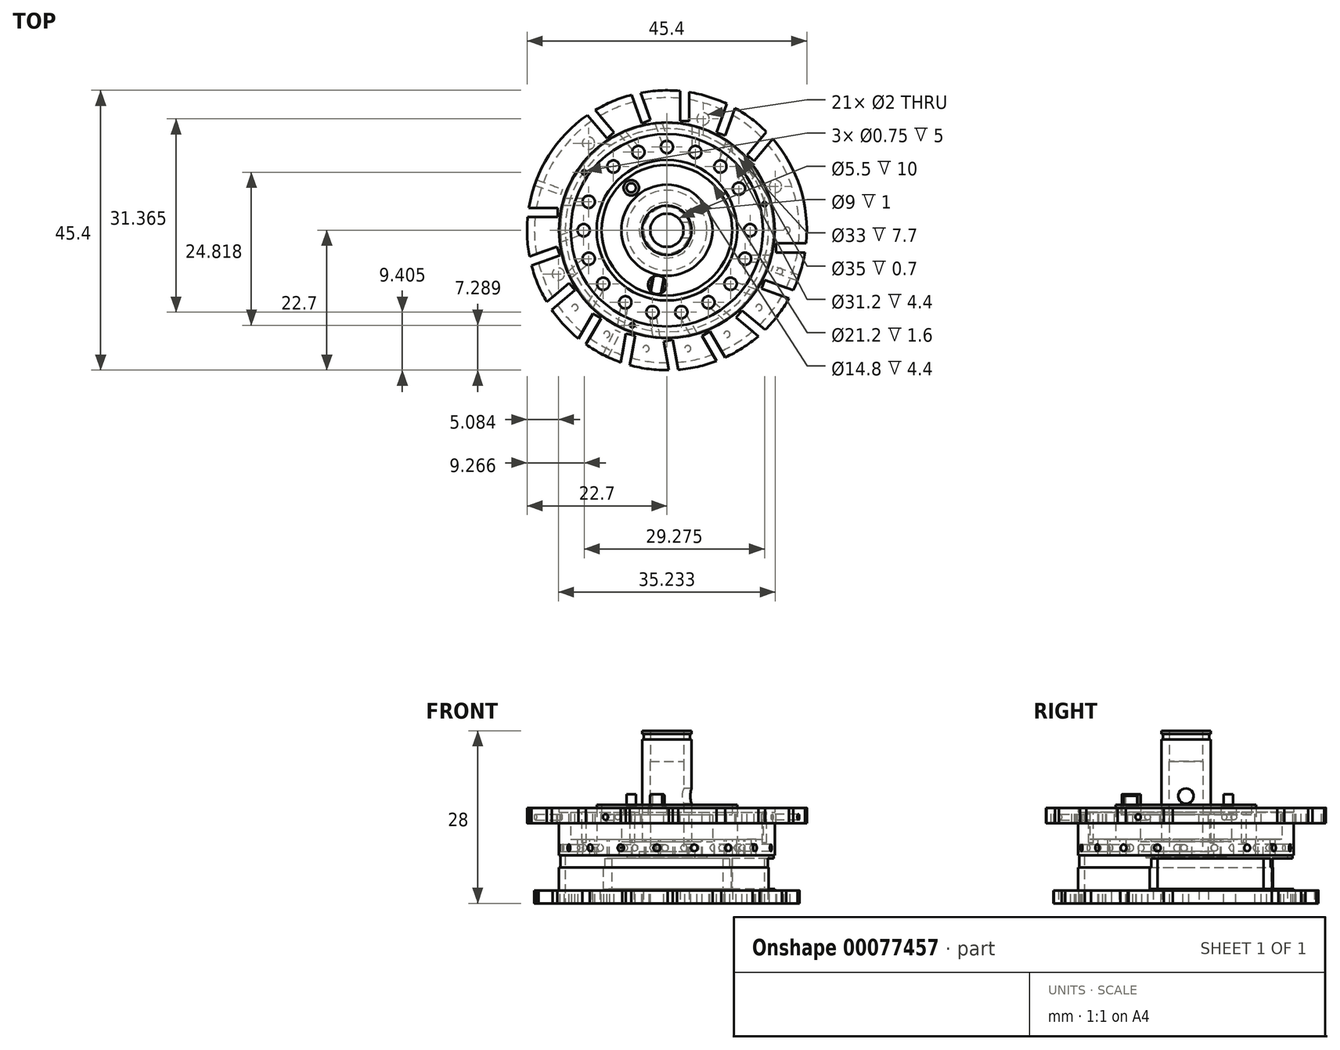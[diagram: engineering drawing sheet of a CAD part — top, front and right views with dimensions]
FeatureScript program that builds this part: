
annotation { "Feature Type Name" : "Feature", "Feature Type Description" : "" }
export const myFeature = defineFeature(function(context is Context, id is Id, definition is map)
    precondition{}
    {
        {
            var Q0;
            Q0=qCreatedBy(makeId("Front.planeOp"),FACE);
            var sketch = newSketch(context, id + "F0", { "sketchPlane" : qUnion([Q0])});
            skLineSegment(sketch, "E0", {"start": v(4, 20.6) * mm, "end": v(4, 20.1) * mm});
            skLineSegment(sketch, "E1", {"start": v(4, 20.1) * mm, "end": v(3.75, 20.1) * mm});
            skLineSegment(sketch, "E2", {"start": v(3.75, 20.1) * mm, "end": v(3.75, 19.2) * mm});
            skLineSegment(sketch, "E3", {"start": v(3.75, 19.2) * mm, "end": v(4, 19.2) * mm});
            skLineSegment(sketch, "E4", {"start": v(4, 19.2) * mm, "end": v(4, 2.6) * mm});
            skLineSegment(sketch, "E5", {"start": v(4, 2.6) * mm, "end": v(7.4, 2.6) * mm});
            skLineSegment(sketch, "E6", {"start": v(7.4, 2.6) * mm, "end": v(7.4, 7) * mm});
            skLineSegment(sketch, "E7", {"start": v(7.4, 7) * mm, "end": v(10.6, 7) * mm});
            skLineSegment(sketch, "E8", {"start": v(10.6, 7) * mm, "end": v(10.6, 8.6) * mm});
            skLineSegment(sketch, "E9", {"start": v(10.6, 8.6) * mm, "end": v(11.4, 8.6) * mm});
            skLineSegment(sketch, "E10", {"start": v(11.4, 8.6) * mm, "end": v(11.4, 3) * mm});
            skLineSegment(sketch, "E11", {"start": v(11.4, 3) * mm, "end": v(15.6, 3) * mm});
            skLineSegment(sketch, "E12", {"start": v(15.6, 3) * mm, "end": v(15.6, 7.4) * mm});
            skLineSegment(sketch, "E13", {"start": v(15.6, 7.4) * mm, "end": v(17.5, 7.4) * mm});
            skLineSegment(sketch, "E14", {"start": v(17.5, 7.4) * mm, "end": v(17.5, 8.1) * mm});
            skLineSegment(sketch, "E15", {"start": v(17.5, 8.1) * mm, "end": v(22.7, 8.1) * mm});
            skLineSegment(sketch, "E16", {"start": v(22.7, 8.1) * mm, "end": v(22.7, 5.6) * mm});
            skLineSegment(sketch, "E17", {"start": v(22.7, 5.6) * mm, "end": v(17.5, 5.6) * mm});
            skLineSegment(sketch, "E18", {"start": v(17.5, 5.6) * mm, "end": v(17.5, 0.4) * mm});
            skLineSegment(sketch, "E19", {"start": v(17.5, 0.4) * mm, "end": v(17.3, 0.4) * mm});
            skLineSegment(sketch, "E20", {"start": v(17.3, 0.4) * mm, "end": v(17.3, -1.6) * mm});
            skLineSegment(sketch, "E21", {"start": v(17.3, -1.6) * mm, "end": v(17.5, -1.6) * mm});
            skLineSegment(sketch, "E22", {"start": v(17.5, -1.6) * mm, "end": v(17.5, -5.3) * mm});
            skLineSegment(sketch, "E23", {"start": v(17.5, -5.3) * mm, "end": v(21.5, -5.3) * mm});
            skLineSegment(sketch, "E24", {"start": v(21.5, -5.3) * mm, "end": v(21.5, -7.4) * mm});
            skLineSegment(sketch, "E25", {"start": v(21.5, -7.4) * mm, "end": v(16.5, -7.4) * mm});
            skLineSegment(sketch, "E26", {"start": v(16.5, -7.4) * mm, "end": v(16.5, 0.3) * mm});
            skLineSegment(sketch, "E27", {"start": v(16.5, 0.3) * mm, "end": v(6.5, 0.3) * mm});
            skLineSegment(sketch, "E28", {"start": v(6.5, 0.3) * mm, "end": v(6.5, 0) * mm});
            skLineSegment(sketch, "E29", {"start": v(6.5, 0) * mm, "end": v(4.5, 0) * mm});
            skLineSegment(sketch, "E30", {"start": v(4.5, 0) * mm, "end": v(4.5, 1) * mm});
            skLineSegment(sketch, "E31", {"start": v(4.5, 1) * mm, "end": v(2.7, 1) * mm});
            skLineSegment(sketch, "E32", {"start": v(2.7, 1) * mm, "end": v(2.7, 5.6) * mm});
            skLineSegment(sketch, "E33", {"start": v(2.7, 5.6) * mm, "end": v(2.75, 5.6) * mm});
            skLineSegment(sketch, "E34", {"start": v(2.75, 5.6) * mm, "end": v(2.75, 15.6) * mm});
            skLineSegment(sketch, "E35", {"start": v(2.75, 15.6) * mm, "end": v(2.7, 15.6) * mm});
            skLineSegment(sketch, "E36", {"start": v(2.7, 15.6) * mm, "end": v(2.7, 20.6) * mm});
            skLineSegment(sketch, "E37", {"start": v(2.7, 20.6) * mm, "end": v(4, 20.6) * mm});
            skLineSegment(sketch, "E38", {"start": v(0, 0) * mm, "end": v(0, 20.6) * mm, "construction": true});
            skSolve(sketch);
        }
        {
            var Q0;
            Q0=makeQuery(id+"F0.imprint","IMPRINT",FACE,{"disambiguationData":[TD([[makeQuery(id+"F0.imprint","IMPRINT",EDGE,{"derivedFrom":sQuery(id+"F0.wireOp",EDGE,"E0")}),-1.0]])]});
            var Q1;
            Q1=sQuery(id+"F0.wireOp",EDGE,"E38");
            revolve(context, id + "F1", {"entities" : qUnion([Q0]), "axis" : qUnion([Q1]), "revolveType" : RevolveType.FULL});
        }
        {
            var Q0;
            Q0=makeQuery(id+"F1.opRevolve","SWEPT_FACE",FACE,{"disambiguationData":[OSD([sQuery(id+"F0.wireOp",EDGE,"E15")])]});
            var sketch = newSketch(context, id + "F2", { "sketchPlane" : qUnion([Q0])});
            skLineSegment(sketch, "E39.bottom", {"start": v(24.7, -2.13) * mm, "end": v(17.7, -2.13) * mm});
            skLineSegment(sketch, "E39.top", {"start": v(24.7, -3.63) * mm, "end": v(17.7, -3.63) * mm});
            skLineSegment(sketch, "E39.left", {"start": v(24.7, -2.13) * mm, "end": v(24.7, -3.63) * mm});
            skLineSegment(sketch, "E39.right", {"start": v(17.7, -2.13) * mm, "end": v(17.7, -3.63) * mm});
            skLineSegment(sketch, "E40", {"start": v(14.9, -4.63) * mm, "end": v(24.7, -4.63) * mm, "construction": true});
            skLineSegment(sketch, "E41", {"start": v(0, 0) * mm, "end": v(21.33, -7.76) * mm, "construction": true});
            skPoint(sketch, "E42", {"position": v(12.69, -4.62) * mm});
            skCircle(sketch, "E43", {"center": v(12.69, -4.62) * mm, "radius": 1 * mm});
            skLineSegment(sketch, "E44", {"start": v(14.9, -4.63) * mm, "end": v(13.69, -4.63) * mm, "construction": true});
            skSolve(sketch);
        }
        {
            var Q0;
            Q0=makeQuery(id+"F2.imprint","IMPRINT",FACE,{"disambiguationData":[TD([[makeQuery(id+"F2.imprint","IMPRINT",EDGE,{"derivedFrom":sQuery(id+"F2.wireOp",EDGE,"E43")}),1.0]])]});
            var Q1;
            {var subQ5=sQuery(id+"F2.wireOp",EDGE,"E39.right");Q1=makeQuery(id+"F2.imprint","IMPRINT",FACE,{"disambiguationData":[TD([[makeQuery(id+"F2.imprint","IMPRINT",EDGE,{"derivedFrom":subQ5}),1.0]])]});}
            extrude(context, id + "F3", {"entities" : qUnion([Q0, Q1]), "oppositeDirection" : true, "depth" : 16 * mm});
        }
        {
            var Q0;
            Q0=makeQuery(id+"F3.opExtrude","SWEPT_BODY",BODY,{"disambiguationData":[OSD([sQuery(id+"F0.wireOp",EDGE,"E15"),sQuery(id+"F0.wireOp",EDGE,"E16"),sQuery(id+"F2.wireOp",EDGE,"E39.bottom"),sQuery(id+"F2.wireOp",EDGE,"E39.top"),sQuery(id+"F2.wireOp",EDGE,"E39.right")])]});
            var Q1;
            Q1=makeQuery(id+"F3.opExtrude","SWEPT_BODY",BODY,{"disambiguationData":[OSD([sQuery(id+"F2.wireOp",EDGE,"E43")])]});
            var Q2;
            Q2=sQuery(id+"F0.wireOp",EDGE,"E38");
            circularPattern(context, id + "F4", {"entities" : qUnion([Q0, Q1]), "axis" : qUnion([Q2]), "angle" : 20 * degree, "instanceCount" : round(10), "oppositeDirection" : true});
        }
        {
            var Q0;
            Q0=makeQuery(id+"F3.opExtrude","SWEPT_BODY",BODY,{"disambiguationData":[OSD([sQuery(id+"F0.wireOp",EDGE,"E15"),sQuery(id+"F0.wireOp",EDGE,"E16"),sQuery(id+"F2.wireOp",EDGE,"E39.bottom"),sQuery(id+"F2.wireOp",EDGE,"E39.top"),sQuery(id+"F2.wireOp",EDGE,"E39.right")])]});
            var Q1;
            Q1=makeQuery(id+"F3.opExtrude","SWEPT_BODY",BODY,{"disambiguationData":[OSD([sQuery(id+"F2.wireOp",EDGE,"E43")])]});
            var Q2;
            Q2=sQuery(id+"F0.wireOp",EDGE,"E38");
            circularPattern(context, id + "F5", {"entities" : qUnion([Q0, Q1]), "axis" : qUnion([Q2]), "angle" : 50 * degree, "instanceCount" : round(2)});
        }
        {
            var Q0;
            Q0=makeQuery(id+"F5.opPattern","COPY",BODY,{"derivedFrom":makeQuery(id+"F3.opExtrude","SWEPT_BODY",BODY,{"disambiguationData":[OSD([sQuery(id+"F2.wireOp",EDGE,"E43")])]}),"instanceName":"1"});
            var Q1;
            Q1=makeQuery(id+"F5.opPattern","COPY",BODY,{"derivedFrom":makeQuery(id+"F3.opExtrude","SWEPT_BODY",BODY,{"disambiguationData":[OSD([sQuery(id+"F0.wireOp",EDGE,"E15"),sQuery(id+"F0.wireOp",EDGE,"E16"),sQuery(id+"F2.wireOp",EDGE,"E39.bottom"),sQuery(id+"F2.wireOp",EDGE,"E39.top"),sQuery(id+"F2.wireOp",EDGE,"E39.right")])]}),"instanceName":"1"});
            var Q2;
            Q2=sQuery(id+"F0.wireOp",EDGE,"E38");
            circularPattern(context, id + "F6", {"entities" : qUnion([Q0, Q1]), "axis" : qUnion([Q2]), "angle" : 20 * degree, "instanceCount" : round(5)});
        }
        {
            var Q0;
            Q0=makeQuery(id+"F6.opPattern","COPY",BODY,{"derivedFrom":makeQuery(id+"F5.opPattern","COPY",BODY,{"derivedFrom":makeQuery(id+"F3.opExtrude","SWEPT_BODY",BODY,{"disambiguationData":[OSD([sQuery(id+"F2.wireOp",EDGE,"E43")])]}),"instanceName":"1"}),"instanceName":"4"});
            var Q1;
            Q1=sQuery(id+"F0.wireOp",EDGE,"E38");
            transform(context, id + "F7", {"entities" : qUnion([Q0]), "transformType" : TransformType.ROTATION, "transformAxis" : qUnion([Q1]), "angle" : 20 * degree, "makeCopy" : true});
        }
        {
            var Q0;
            Q0=makeQuery(id+"F3.opExtrude","SWEPT_BODY",BODY,{"disambiguationData":[OSD([sQuery(id+"F0.wireOp",EDGE,"E15"),sQuery(id+"F0.wireOp",EDGE,"E16"),sQuery(id+"F2.wireOp",EDGE,"E39.bottom"),sQuery(id+"F2.wireOp",EDGE,"E39.top"),sQuery(id+"F2.wireOp",EDGE,"E39.right")])]});
            var Q1;
            Q1=makeQuery(id+"F3.opExtrude","SWEPT_BODY",BODY,{"disambiguationData":[OSD([sQuery(id+"F2.wireOp",EDGE,"E43")])]});
            var Q2;
            Q2=makeQuery(id+"F4.opPattern","COPY",BODY,{"derivedFrom":makeQuery(id+"F3.opExtrude","SWEPT_BODY",BODY,{"disambiguationData":[OSD([sQuery(id+"F0.wireOp",EDGE,"E15"),sQuery(id+"F0.wireOp",EDGE,"E16"),sQuery(id+"F2.wireOp",EDGE,"E39.bottom"),sQuery(id+"F2.wireOp",EDGE,"E39.top"),sQuery(id+"F2.wireOp",EDGE,"E39.right")])]}),"instanceName":"1"});
            var Q3;
            Q3=makeQuery(id+"F4.opPattern","COPY",BODY,{"derivedFrom":makeQuery(id+"F3.opExtrude","SWEPT_BODY",BODY,{"disambiguationData":[OSD([sQuery(id+"F2.wireOp",EDGE,"E43")])]}),"instanceName":"1"});
            var Q4;
            Q4=makeQuery(id+"F4.opPattern","COPY",BODY,{"derivedFrom":makeQuery(id+"F3.opExtrude","SWEPT_BODY",BODY,{"disambiguationData":[OSD([sQuery(id+"F0.wireOp",EDGE,"E15"),sQuery(id+"F0.wireOp",EDGE,"E16"),sQuery(id+"F2.wireOp",EDGE,"E39.bottom"),sQuery(id+"F2.wireOp",EDGE,"E39.top"),sQuery(id+"F2.wireOp",EDGE,"E39.right")])]}),"instanceName":"2"});
            var Q5;
            Q5=makeQuery(id+"F4.opPattern","COPY",BODY,{"derivedFrom":makeQuery(id+"F3.opExtrude","SWEPT_BODY",BODY,{"disambiguationData":[OSD([sQuery(id+"F2.wireOp",EDGE,"E43")])]}),"instanceName":"2"});
            var Q6;
            Q6=makeQuery(id+"F4.opPattern","COPY",BODY,{"derivedFrom":makeQuery(id+"F3.opExtrude","SWEPT_BODY",BODY,{"disambiguationData":[OSD([sQuery(id+"F0.wireOp",EDGE,"E15"),sQuery(id+"F0.wireOp",EDGE,"E16"),sQuery(id+"F2.wireOp",EDGE,"E39.bottom"),sQuery(id+"F2.wireOp",EDGE,"E39.top"),sQuery(id+"F2.wireOp",EDGE,"E39.right")])]}),"instanceName":"3"});
            var Q7;
            Q7=makeQuery(id+"F4.opPattern","COPY",BODY,{"derivedFrom":makeQuery(id+"F3.opExtrude","SWEPT_BODY",BODY,{"disambiguationData":[OSD([sQuery(id+"F2.wireOp",EDGE,"E43")])]}),"instanceName":"3"});
            var Q8;
            Q8=makeQuery(id+"F4.opPattern","COPY",BODY,{"derivedFrom":makeQuery(id+"F3.opExtrude","SWEPT_BODY",BODY,{"disambiguationData":[OSD([sQuery(id+"F0.wireOp",EDGE,"E15"),sQuery(id+"F0.wireOp",EDGE,"E16"),sQuery(id+"F2.wireOp",EDGE,"E39.bottom"),sQuery(id+"F2.wireOp",EDGE,"E39.top"),sQuery(id+"F2.wireOp",EDGE,"E39.right")])]}),"instanceName":"4"});
            var Q9;
            Q9=makeQuery(id+"F4.opPattern","COPY",BODY,{"derivedFrom":makeQuery(id+"F3.opExtrude","SWEPT_BODY",BODY,{"disambiguationData":[OSD([sQuery(id+"F2.wireOp",EDGE,"E43")])]}),"instanceName":"4"});
            var Q10;
            Q10=makeQuery(id+"F4.opPattern","COPY",BODY,{"derivedFrom":makeQuery(id+"F3.opExtrude","SWEPT_BODY",BODY,{"disambiguationData":[OSD([sQuery(id+"F0.wireOp",EDGE,"E15"),sQuery(id+"F0.wireOp",EDGE,"E16"),sQuery(id+"F2.wireOp",EDGE,"E39.bottom"),sQuery(id+"F2.wireOp",EDGE,"E39.top"),sQuery(id+"F2.wireOp",EDGE,"E39.right")])]}),"instanceName":"5"});
            var Q11;
            Q11=makeQuery(id+"F4.opPattern","COPY",BODY,{"derivedFrom":makeQuery(id+"F3.opExtrude","SWEPT_BODY",BODY,{"disambiguationData":[OSD([sQuery(id+"F2.wireOp",EDGE,"E43")])]}),"instanceName":"5"});
            var Q12;
            Q12=makeQuery(id+"F4.opPattern","COPY",BODY,{"derivedFrom":makeQuery(id+"F3.opExtrude","SWEPT_BODY",BODY,{"disambiguationData":[OSD([sQuery(id+"F0.wireOp",EDGE,"E15"),sQuery(id+"F0.wireOp",EDGE,"E16"),sQuery(id+"F2.wireOp",EDGE,"E39.bottom"),sQuery(id+"F2.wireOp",EDGE,"E39.top"),sQuery(id+"F2.wireOp",EDGE,"E39.right")])]}),"instanceName":"6"});
            var Q13;
            Q13=makeQuery(id+"F4.opPattern","COPY",BODY,{"derivedFrom":makeQuery(id+"F3.opExtrude","SWEPT_BODY",BODY,{"disambiguationData":[OSD([sQuery(id+"F2.wireOp",EDGE,"E43")])]}),"instanceName":"6"});
            var Q14;
            Q14=makeQuery(id+"F4.opPattern","COPY",BODY,{"derivedFrom":makeQuery(id+"F3.opExtrude","SWEPT_BODY",BODY,{"disambiguationData":[OSD([sQuery(id+"F0.wireOp",EDGE,"E15"),sQuery(id+"F0.wireOp",EDGE,"E16"),sQuery(id+"F2.wireOp",EDGE,"E39.bottom"),sQuery(id+"F2.wireOp",EDGE,"E39.top"),sQuery(id+"F2.wireOp",EDGE,"E39.right")])]}),"instanceName":"7"});
            var Q15;
            Q15=makeQuery(id+"F4.opPattern","COPY",BODY,{"derivedFrom":makeQuery(id+"F3.opExtrude","SWEPT_BODY",BODY,{"disambiguationData":[OSD([sQuery(id+"F2.wireOp",EDGE,"E43")])]}),"instanceName":"7"});
            var Q16;
            Q16=makeQuery(id+"F4.opPattern","COPY",BODY,{"derivedFrom":makeQuery(id+"F3.opExtrude","SWEPT_BODY",BODY,{"disambiguationData":[OSD([sQuery(id+"F0.wireOp",EDGE,"E15"),sQuery(id+"F0.wireOp",EDGE,"E16"),sQuery(id+"F2.wireOp",EDGE,"E39.bottom"),sQuery(id+"F2.wireOp",EDGE,"E39.top"),sQuery(id+"F2.wireOp",EDGE,"E39.right")])]}),"instanceName":"8"});
            var Q17;
            Q17=makeQuery(id+"F4.opPattern","COPY",BODY,{"derivedFrom":makeQuery(id+"F3.opExtrude","SWEPT_BODY",BODY,{"disambiguationData":[OSD([sQuery(id+"F2.wireOp",EDGE,"E43")])]}),"instanceName":"8"});
            var Q18;
            Q18=makeQuery(id+"F4.opPattern","COPY",BODY,{"derivedFrom":makeQuery(id+"F3.opExtrude","SWEPT_BODY",BODY,{"disambiguationData":[OSD([sQuery(id+"F0.wireOp",EDGE,"E15"),sQuery(id+"F0.wireOp",EDGE,"E16"),sQuery(id+"F2.wireOp",EDGE,"E39.bottom"),sQuery(id+"F2.wireOp",EDGE,"E39.top"),sQuery(id+"F2.wireOp",EDGE,"E39.right")])]}),"instanceName":"9"});
            var Q19;
            Q19=makeQuery(id+"F4.opPattern","COPY",BODY,{"derivedFrom":makeQuery(id+"F3.opExtrude","SWEPT_BODY",BODY,{"disambiguationData":[OSD([sQuery(id+"F2.wireOp",EDGE,"E43")])]}),"instanceName":"9"});
            var Q20;
            Q20=makeQuery(id+"F5.opPattern","COPY",BODY,{"derivedFrom":makeQuery(id+"F3.opExtrude","SWEPT_BODY",BODY,{"disambiguationData":[OSD([sQuery(id+"F0.wireOp",EDGE,"E15"),sQuery(id+"F0.wireOp",EDGE,"E16"),sQuery(id+"F2.wireOp",EDGE,"E39.bottom"),sQuery(id+"F2.wireOp",EDGE,"E39.top"),sQuery(id+"F2.wireOp",EDGE,"E39.right")])]}),"instanceName":"1"});
            var Q21;
            Q21=makeQuery(id+"F5.opPattern","COPY",BODY,{"derivedFrom":makeQuery(id+"F3.opExtrude","SWEPT_BODY",BODY,{"disambiguationData":[OSD([sQuery(id+"F2.wireOp",EDGE,"E43")])]}),"instanceName":"1"});
            var Q22;
            Q22=makeQuery(id+"F6.opPattern","COPY",BODY,{"derivedFrom":makeQuery(id+"F5.opPattern","COPY",BODY,{"derivedFrom":makeQuery(id+"F3.opExtrude","SWEPT_BODY",BODY,{"disambiguationData":[OSD([sQuery(id+"F0.wireOp",EDGE,"E15"),sQuery(id+"F0.wireOp",EDGE,"E16"),sQuery(id+"F2.wireOp",EDGE,"E39.bottom"),sQuery(id+"F2.wireOp",EDGE,"E39.top"),sQuery(id+"F2.wireOp",EDGE,"E39.right")])]}),"instanceName":"1"}),"instanceName":"1"});
            var Q23;
            Q23=makeQuery(id+"F6.opPattern","COPY",BODY,{"derivedFrom":makeQuery(id+"F5.opPattern","COPY",BODY,{"derivedFrom":makeQuery(id+"F3.opExtrude","SWEPT_BODY",BODY,{"disambiguationData":[OSD([sQuery(id+"F2.wireOp",EDGE,"E43")])]}),"instanceName":"1"}),"instanceName":"1"});
            var Q24;
            Q24=makeQuery(id+"F6.opPattern","COPY",BODY,{"derivedFrom":makeQuery(id+"F5.opPattern","COPY",BODY,{"derivedFrom":makeQuery(id+"F3.opExtrude","SWEPT_BODY",BODY,{"disambiguationData":[OSD([sQuery(id+"F0.wireOp",EDGE,"E15"),sQuery(id+"F0.wireOp",EDGE,"E16"),sQuery(id+"F2.wireOp",EDGE,"E39.bottom"),sQuery(id+"F2.wireOp",EDGE,"E39.top"),sQuery(id+"F2.wireOp",EDGE,"E39.right")])]}),"instanceName":"1"}),"instanceName":"2"});
            var Q25;
            Q25=makeQuery(id+"F6.opPattern","COPY",BODY,{"derivedFrom":makeQuery(id+"F5.opPattern","COPY",BODY,{"derivedFrom":makeQuery(id+"F3.opExtrude","SWEPT_BODY",BODY,{"disambiguationData":[OSD([sQuery(id+"F2.wireOp",EDGE,"E43")])]}),"instanceName":"1"}),"instanceName":"2"});
            var Q26;
            Q26=makeQuery(id+"F6.opPattern","COPY",BODY,{"derivedFrom":makeQuery(id+"F5.opPattern","COPY",BODY,{"derivedFrom":makeQuery(id+"F3.opExtrude","SWEPT_BODY",BODY,{"disambiguationData":[OSD([sQuery(id+"F0.wireOp",EDGE,"E15"),sQuery(id+"F0.wireOp",EDGE,"E16"),sQuery(id+"F2.wireOp",EDGE,"E39.bottom"),sQuery(id+"F2.wireOp",EDGE,"E39.top"),sQuery(id+"F2.wireOp",EDGE,"E39.right")])]}),"instanceName":"1"}),"instanceName":"3"});
            var Q27;
            Q27=makeQuery(id+"F6.opPattern","COPY",BODY,{"derivedFrom":makeQuery(id+"F5.opPattern","COPY",BODY,{"derivedFrom":makeQuery(id+"F3.opExtrude","SWEPT_BODY",BODY,{"disambiguationData":[OSD([sQuery(id+"F2.wireOp",EDGE,"E43")])]}),"instanceName":"1"}),"instanceName":"3"});
            var Q28;
            Q28=makeQuery(id+"F6.opPattern","COPY",BODY,{"derivedFrom":makeQuery(id+"F5.opPattern","COPY",BODY,{"derivedFrom":makeQuery(id+"F3.opExtrude","SWEPT_BODY",BODY,{"disambiguationData":[OSD([sQuery(id+"F0.wireOp",EDGE,"E15"),sQuery(id+"F0.wireOp",EDGE,"E16"),sQuery(id+"F2.wireOp",EDGE,"E39.bottom"),sQuery(id+"F2.wireOp",EDGE,"E39.top"),sQuery(id+"F2.wireOp",EDGE,"E39.right")])]}),"instanceName":"1"}),"instanceName":"4"});
            var Q29;
            Q29=makeQuery(id+"F6.opPattern","COPY",BODY,{"derivedFrom":makeQuery(id+"F5.opPattern","COPY",BODY,{"derivedFrom":makeQuery(id+"F3.opExtrude","SWEPT_BODY",BODY,{"disambiguationData":[OSD([sQuery(id+"F2.wireOp",EDGE,"E43")])]}),"instanceName":"1"}),"instanceName":"4"});
            var Q30;
            Q30=makeQuery(id+"F6.opPattern","COPY",BODY,{"derivedFrom":makeQuery(id+"F5.opPattern","COPY",BODY,{"derivedFrom":makeQuery(id+"F3.opExtrude","SWEPT_BODY",BODY,{"disambiguationData":[OSD([sQuery(id+"F0.wireOp",EDGE,"E15"),sQuery(id+"F0.wireOp",EDGE,"E16"),sQuery(id+"F2.wireOp",EDGE,"E39.bottom"),sQuery(id+"F2.wireOp",EDGE,"E39.top"),sQuery(id+"F2.wireOp",EDGE,"E39.right")])]}),"instanceName":"1"}),"instanceName":"5"});
            var Q31;
            Q31=makeQuery(id+"F6.opPattern","COPY",BODY,{"derivedFrom":makeQuery(id+"F5.opPattern","COPY",BODY,{"derivedFrom":makeQuery(id+"F3.opExtrude","SWEPT_BODY",BODY,{"disambiguationData":[OSD([sQuery(id+"F2.wireOp",EDGE,"E43")])]}),"instanceName":"1"}),"instanceName":"5"});
            var Q32;
            Q32=makeQuery(id+"F7.opPattern","COPY",BODY,{"derivedFrom":makeQuery(id+"F6.opPattern","COPY",BODY,{"derivedFrom":makeQuery(id+"F5.opPattern","COPY",BODY,{"derivedFrom":makeQuery(id+"F3.opExtrude","SWEPT_BODY",BODY,{"disambiguationData":[OSD([sQuery(id+"F2.wireOp",EDGE,"E43")])]}),"instanceName":"1"}),"instanceName":"4"}),"instanceName":"1"});
            var Q33;
            Q33=makeQuery(id+"F1.opRevolve","SWEPT_BODY",BODY,{"disambiguationData":[OSD([sQuery(id+"F0.wireOp",EDGE,"E0"),sQuery(id+"F0.wireOp",EDGE,"E1"),sQuery(id+"F0.wireOp",EDGE,"E2"),sQuery(id+"F0.wireOp",EDGE,"E3"),sQuery(id+"F0.wireOp",EDGE,"E4"),sQuery(id+"F0.wireOp",EDGE,"E5"),sQuery(id+"F0.wireOp",EDGE,"E6"),sQuery(id+"F0.wireOp",EDGE,"E7"),sQuery(id+"F0.wireOp",EDGE,"E8"),sQuery(id+"F0.wireOp",EDGE,"E9"),sQuery(id+"F0.wireOp",EDGE,"E10"),sQuery(id+"F0.wireOp",EDGE,"E11"),sQuery(id+"F0.wireOp",EDGE,"E12"),sQuery(id+"F0.wireOp",EDGE,"E13"),sQuery(id+"F0.wireOp",EDGE,"E14"),sQuery(id+"F0.wireOp",EDGE,"E15"),sQuery(id+"F0.wireOp",EDGE,"E16"),sQuery(id+"F0.wireOp",EDGE,"E17"),sQuery(id+"F0.wireOp",EDGE,"E18"),sQuery(id+"F0.wireOp",EDGE,"E19"),sQuery(id+"F0.wireOp",EDGE,"E20"),sQuery(id+"F0.wireOp",EDGE,"E21"),sQuery(id+"F0.wireOp",EDGE,"E22"),sQuery(id+"F0.wireOp",EDGE,"E23"),sQuery(id+"F0.wireOp",EDGE,"E24"),sQuery(id+"F0.wireOp",EDGE,"E25"),sQuery(id+"F0.wireOp",EDGE,"E26"),sQuery(id+"F0.wireOp",EDGE,"E27"),sQuery(id+"F0.wireOp",EDGE,"E28"),sQuery(id+"F0.wireOp",EDGE,"E29"),sQuery(id+"F0.wireOp",EDGE,"E30"),sQuery(id+"F0.wireOp",EDGE,"E31"),sQuery(id+"F0.wireOp",EDGE,"E32"),sQuery(id+"F0.wireOp",EDGE,"E33"),sQuery(id+"F0.wireOp",EDGE,"E34"),sQuery(id+"F0.wireOp",EDGE,"E35"),sQuery(id+"F0.wireOp",EDGE,"E36"),sQuery(id+"F0.wireOp",EDGE,"E37")])]});
            booleanBodies(context, id + "F8", {"operationType" : BooleanOperationType.SUBTRACTION, "tools" : qUnion([Q0, Q1, Q2, Q3, Q4, Q5, Q6, Q7, Q8, Q9, Q10, Q11, Q12, Q13, Q14, Q15, Q16, Q17, Q18, Q19, Q20, Q21, Q22, Q23, Q24, Q25, Q26, Q27, Q28, Q29, Q30, Q31, Q32]), "targets" : qUnion([Q33])});
        }
        {
            var Q0;
            Q0=makeQuery(id+"F1.opRevolve","SWEPT_FACE",FACE,{"disambiguationData":[OSD([sQuery(id+"F0.wireOp",EDGE,"E9")])]});
            cPlane(context, id + "F9", {"entities" : qUnion([Q0]), "cplaneType" : CPlaneType.OFFSET, "offset" : 7 * mm, "oppositeDirection" : true, "width" : 150 * mm, "height" : 150 * mm});
        }
        {
            var Q0;
            Q0=qCreatedBy(id+"F9.planeOp",FACE);
            var sketch = newSketch(context, id + "F10", { "sketchPlane" : qUnion([Q0])});
            skLineSegment(sketch, "E45", {"start": v(23.53, -4.63) * mm, "end": v(13.53, -4.63) * mm, "construction": true});
            skLineSegment(sketch, "E46", {"start": v(0, 0) * mm, "end": v(12.69, -4.62) * mm, "construction": true});
            skCircle(sketch, "E47", {"center": v(12.69, -4.62) * mm, "radius": 1 * mm, "construction": true});
            skLineSegment(sketch, "E48.bottom", {"start": v(13.53, -4.63) * mm, "end": v(23.53, -4.63) * mm});
            skLineSegment(sketch, "E48.top", {"start": v(13.53, -4.08) * mm, "end": v(23.53, -4.08) * mm});
            skLineSegment(sketch, "E48.left", {"start": v(13.53, -4.63) * mm, "end": v(13.53, -4.08) * mm});
            skLineSegment(sketch, "E48.right", {"start": v(23.53, -4.63) * mm, "end": v(23.53, -4.08) * mm});
            skSolve(sketch);
        }
        {
            var Q0;
            Q0=makeQuery(id+"F10.imprint","IMPRINT",FACE,{"disambiguationData":[TD([[makeQuery(id+"F10.imprint","IMPRINT",EDGE,{"derivedFrom":sQuery(id+"F10.wireOp",EDGE,"E48.bottom")}),1.0]])]});
            var Q1;
            Q1=sQuery(id+"F10.wireOp",EDGE,"E48.bottom");
            revolve(context, id + "F11", {"entities" : qUnion([Q0]), "axis" : qUnion([Q1]), "revolveType" : RevolveType.FULL});
        }
        {
            var Q0;
            Q0=makeQuery(id+"F11.opRevolve","SWEPT_BODY",BODY,{"disambiguationData":[OSD([sQuery(id+"F10.wireOp",EDGE,"E48.bottom"),sQuery(id+"F10.wireOp",EDGE,"E48.top"),sQuery(id+"F10.wireOp",EDGE,"E48.left"),sQuery(id+"F10.wireOp",EDGE,"E48.right")])]});
            var Q1;
            Q1=sQuery(id+"F0.wireOp",EDGE,"E38");
            circularPattern(context, id + "F12", {"entities" : qUnion([Q0]), "axis" : qUnion([Q1]), "angle" : 20 * degree, "instanceCount" : round(10), "oppositeDirection" : true});
        }
        {
            var Q0;
            Q0=makeQuery(id+"F11.opRevolve","SWEPT_BODY",BODY,{"disambiguationData":[OSD([sQuery(id+"F10.wireOp",EDGE,"E48.bottom"),sQuery(id+"F10.wireOp",EDGE,"E48.top"),sQuery(id+"F10.wireOp",EDGE,"E48.left"),sQuery(id+"F10.wireOp",EDGE,"E48.right")])]});
            var Q1;
            Q1=sQuery(id+"F0.wireOp",EDGE,"E38");
            circularPattern(context, id + "F13", {"entities" : qUnion([Q0]), "axis" : qUnion([Q1]), "angle" : 50 * degree, "instanceCount" : 2});
        }
        {
            var Q0;
            Q0=makeQuery(id+"F13.opPattern","COPY",BODY,{"derivedFrom":makeQuery(id+"F11.opRevolve","SWEPT_BODY",BODY,{"disambiguationData":[OSD([sQuery(id+"F10.wireOp",EDGE,"E48.bottom"),sQuery(id+"F10.wireOp",EDGE,"E48.top"),sQuery(id+"F10.wireOp",EDGE,"E48.left"),sQuery(id+"F10.wireOp",EDGE,"E48.right")])]}),"instanceName":"1"});
            var Q1;
            Q1=sQuery(id+"F0.wireOp",EDGE,"E38");
            circularPattern(context, id + "F14", {"entities" : qUnion([Q0]), "axis" : qUnion([Q1]), "angle" : 20 * degree, "instanceCount" : round(5)});
        }
        {
            var Q0;
            Q0=makeQuery(id+"F11.opRevolve","SWEPT_BODY",BODY,{"disambiguationData":[OSD([sQuery(id+"F10.wireOp",EDGE,"E48.bottom"),sQuery(id+"F10.wireOp",EDGE,"E48.top"),sQuery(id+"F10.wireOp",EDGE,"E48.left"),sQuery(id+"F10.wireOp",EDGE,"E48.right")])]});
            var Q1;
            Q1=makeQuery(id+"F12.opPattern","COPY",BODY,{"derivedFrom":makeQuery(id+"F11.opRevolve","SWEPT_BODY",BODY,{"disambiguationData":[OSD([sQuery(id+"F10.wireOp",EDGE,"E48.bottom"),sQuery(id+"F10.wireOp",EDGE,"E48.top"),sQuery(id+"F10.wireOp",EDGE,"E48.left"),sQuery(id+"F10.wireOp",EDGE,"E48.right")])]}),"instanceName":"1"});
            var Q2;
            Q2=makeQuery(id+"F12.opPattern","COPY",BODY,{"derivedFrom":makeQuery(id+"F11.opRevolve","SWEPT_BODY",BODY,{"disambiguationData":[OSD([sQuery(id+"F10.wireOp",EDGE,"E48.bottom"),sQuery(id+"F10.wireOp",EDGE,"E48.top"),sQuery(id+"F10.wireOp",EDGE,"E48.left"),sQuery(id+"F10.wireOp",EDGE,"E48.right")])]}),"instanceName":"2"});
            var Q3;
            Q3=makeQuery(id+"F12.opPattern","COPY",BODY,{"derivedFrom":makeQuery(id+"F11.opRevolve","SWEPT_BODY",BODY,{"disambiguationData":[OSD([sQuery(id+"F10.wireOp",EDGE,"E48.bottom"),sQuery(id+"F10.wireOp",EDGE,"E48.top"),sQuery(id+"F10.wireOp",EDGE,"E48.left"),sQuery(id+"F10.wireOp",EDGE,"E48.right")])]}),"instanceName":"3"});
            var Q4;
            Q4=makeQuery(id+"F12.opPattern","COPY",BODY,{"derivedFrom":makeQuery(id+"F11.opRevolve","SWEPT_BODY",BODY,{"disambiguationData":[OSD([sQuery(id+"F10.wireOp",EDGE,"E48.bottom"),sQuery(id+"F10.wireOp",EDGE,"E48.top"),sQuery(id+"F10.wireOp",EDGE,"E48.left"),sQuery(id+"F10.wireOp",EDGE,"E48.right")])]}),"instanceName":"4"});
            var Q5;
            Q5=makeQuery(id+"F12.opPattern","COPY",BODY,{"derivedFrom":makeQuery(id+"F11.opRevolve","SWEPT_BODY",BODY,{"disambiguationData":[OSD([sQuery(id+"F10.wireOp",EDGE,"E48.bottom"),sQuery(id+"F10.wireOp",EDGE,"E48.top"),sQuery(id+"F10.wireOp",EDGE,"E48.left"),sQuery(id+"F10.wireOp",EDGE,"E48.right")])]}),"instanceName":"5"});
            var Q6;
            Q6=makeQuery(id+"F12.opPattern","COPY",BODY,{"derivedFrom":makeQuery(id+"F11.opRevolve","SWEPT_BODY",BODY,{"disambiguationData":[OSD([sQuery(id+"F10.wireOp",EDGE,"E48.bottom"),sQuery(id+"F10.wireOp",EDGE,"E48.top"),sQuery(id+"F10.wireOp",EDGE,"E48.left"),sQuery(id+"F10.wireOp",EDGE,"E48.right")])]}),"instanceName":"6"});
            var Q7;
            Q7=makeQuery(id+"F12.opPattern","COPY",BODY,{"derivedFrom":makeQuery(id+"F11.opRevolve","SWEPT_BODY",BODY,{"disambiguationData":[OSD([sQuery(id+"F10.wireOp",EDGE,"E48.bottom"),sQuery(id+"F10.wireOp",EDGE,"E48.top"),sQuery(id+"F10.wireOp",EDGE,"E48.left"),sQuery(id+"F10.wireOp",EDGE,"E48.right")])]}),"instanceName":"7"});
            var Q8;
            Q8=makeQuery(id+"F12.opPattern","COPY",BODY,{"derivedFrom":makeQuery(id+"F11.opRevolve","SWEPT_BODY",BODY,{"disambiguationData":[OSD([sQuery(id+"F10.wireOp",EDGE,"E48.bottom"),sQuery(id+"F10.wireOp",EDGE,"E48.top"),sQuery(id+"F10.wireOp",EDGE,"E48.left"),sQuery(id+"F10.wireOp",EDGE,"E48.right")])]}),"instanceName":"8"});
            var Q9;
            Q9=makeQuery(id+"F12.opPattern","COPY",BODY,{"derivedFrom":makeQuery(id+"F11.opRevolve","SWEPT_BODY",BODY,{"disambiguationData":[OSD([sQuery(id+"F10.wireOp",EDGE,"E48.bottom"),sQuery(id+"F10.wireOp",EDGE,"E48.top"),sQuery(id+"F10.wireOp",EDGE,"E48.left"),sQuery(id+"F10.wireOp",EDGE,"E48.right")])]}),"instanceName":"9"});
            var Q10;
            Q10=makeQuery(id+"F13.opPattern","COPY",BODY,{"derivedFrom":makeQuery(id+"F11.opRevolve","SWEPT_BODY",BODY,{"disambiguationData":[OSD([sQuery(id+"F10.wireOp",EDGE,"E48.bottom"),sQuery(id+"F10.wireOp",EDGE,"E48.top"),sQuery(id+"F10.wireOp",EDGE,"E48.left"),sQuery(id+"F10.wireOp",EDGE,"E48.right")])]}),"instanceName":"1"});
            var Q11;
            Q11=makeQuery(id+"F14.opPattern","COPY",BODY,{"derivedFrom":makeQuery(id+"F13.opPattern","COPY",BODY,{"derivedFrom":makeQuery(id+"F11.opRevolve","SWEPT_BODY",BODY,{"disambiguationData":[OSD([sQuery(id+"F10.wireOp",EDGE,"E48.bottom"),sQuery(id+"F10.wireOp",EDGE,"E48.top"),sQuery(id+"F10.wireOp",EDGE,"E48.left"),sQuery(id+"F10.wireOp",EDGE,"E48.right")])]}),"instanceName":"1"}),"instanceName":"1"});
            var Q12;
            Q12=makeQuery(id+"F14.opPattern","COPY",BODY,{"derivedFrom":makeQuery(id+"F13.opPattern","COPY",BODY,{"derivedFrom":makeQuery(id+"F11.opRevolve","SWEPT_BODY",BODY,{"disambiguationData":[OSD([sQuery(id+"F10.wireOp",EDGE,"E48.bottom"),sQuery(id+"F10.wireOp",EDGE,"E48.top"),sQuery(id+"F10.wireOp",EDGE,"E48.left"),sQuery(id+"F10.wireOp",EDGE,"E48.right")])]}),"instanceName":"1"}),"instanceName":"2"});
            var Q13;
            Q13=makeQuery(id+"F14.opPattern","COPY",BODY,{"derivedFrom":makeQuery(id+"F13.opPattern","COPY",BODY,{"derivedFrom":makeQuery(id+"F11.opRevolve","SWEPT_BODY",BODY,{"disambiguationData":[OSD([sQuery(id+"F10.wireOp",EDGE,"E48.bottom"),sQuery(id+"F10.wireOp",EDGE,"E48.top"),sQuery(id+"F10.wireOp",EDGE,"E48.left"),sQuery(id+"F10.wireOp",EDGE,"E48.right")])]}),"instanceName":"1"}),"instanceName":"3"});
            var Q14;
            Q14=makeQuery(id+"F14.opPattern","COPY",BODY,{"derivedFrom":makeQuery(id+"F13.opPattern","COPY",BODY,{"derivedFrom":makeQuery(id+"F11.opRevolve","SWEPT_BODY",BODY,{"disambiguationData":[OSD([sQuery(id+"F10.wireOp",EDGE,"E48.bottom"),sQuery(id+"F10.wireOp",EDGE,"E48.top"),sQuery(id+"F10.wireOp",EDGE,"E48.left"),sQuery(id+"F10.wireOp",EDGE,"E48.right")])]}),"instanceName":"1"}),"instanceName":"4"});
            var Q15;
            Q15=makeQuery(id+"F14.opPattern","COPY",BODY,{"derivedFrom":makeQuery(id+"F13.opPattern","COPY",BODY,{"derivedFrom":makeQuery(id+"F11.opRevolve","SWEPT_BODY",BODY,{"disambiguationData":[OSD([sQuery(id+"F10.wireOp",EDGE,"E48.bottom"),sQuery(id+"F10.wireOp",EDGE,"E48.top"),sQuery(id+"F10.wireOp",EDGE,"E48.left"),sQuery(id+"F10.wireOp",EDGE,"E48.right")])]}),"instanceName":"1"}),"instanceName":"5"});
            var Q16;
            Q16=makeQuery(id+"F1.opRevolve","SWEPT_BODY",BODY,{"disambiguationData":[OSD([sQuery(id+"F0.wireOp",EDGE,"E0"),sQuery(id+"F0.wireOp",EDGE,"E1"),sQuery(id+"F0.wireOp",EDGE,"E2"),sQuery(id+"F0.wireOp",EDGE,"E3"),sQuery(id+"F0.wireOp",EDGE,"E4"),sQuery(id+"F0.wireOp",EDGE,"E5"),sQuery(id+"F0.wireOp",EDGE,"E6"),sQuery(id+"F0.wireOp",EDGE,"E7"),sQuery(id+"F0.wireOp",EDGE,"E8"),sQuery(id+"F0.wireOp",EDGE,"E9"),sQuery(id+"F0.wireOp",EDGE,"E10"),sQuery(id+"F0.wireOp",EDGE,"E11"),sQuery(id+"F0.wireOp",EDGE,"E12"),sQuery(id+"F0.wireOp",EDGE,"E13"),sQuery(id+"F0.wireOp",EDGE,"E14"),sQuery(id+"F0.wireOp",EDGE,"E15"),sQuery(id+"F0.wireOp",EDGE,"E16"),sQuery(id+"F0.wireOp",EDGE,"E17"),sQuery(id+"F0.wireOp",EDGE,"E18"),sQuery(id+"F0.wireOp",EDGE,"E19"),sQuery(id+"F0.wireOp",EDGE,"E20"),sQuery(id+"F0.wireOp",EDGE,"E21"),sQuery(id+"F0.wireOp",EDGE,"E22"),sQuery(id+"F0.wireOp",EDGE,"E23"),sQuery(id+"F0.wireOp",EDGE,"E24"),sQuery(id+"F0.wireOp",EDGE,"E25"),sQuery(id+"F0.wireOp",EDGE,"E26"),sQuery(id+"F0.wireOp",EDGE,"E27"),sQuery(id+"F0.wireOp",EDGE,"E28"),sQuery(id+"F0.wireOp",EDGE,"E29"),sQuery(id+"F0.wireOp",EDGE,"E30"),sQuery(id+"F0.wireOp",EDGE,"E31"),sQuery(id+"F0.wireOp",EDGE,"E32"),sQuery(id+"F0.wireOp",EDGE,"E33"),sQuery(id+"F0.wireOp",EDGE,"E34"),sQuery(id+"F0.wireOp",EDGE,"E35"),sQuery(id+"F0.wireOp",EDGE,"E36"),sQuery(id+"F0.wireOp",EDGE,"E37")])]});
            booleanBodies(context, id + "F15", {"operationType" : BooleanOperationType.SUBTRACTION, "tools" : qUnion([Q0, Q1, Q2, Q3, Q4, Q5, Q6, Q7, Q8, Q9, Q10, Q11, Q12, Q13, Q14, Q15]), "targets" : qUnion([Q16])});
        }
        {
            var Q0;
            Q0=makeQuery(id+"F1.opRevolve","SWEPT_FACE",FACE,{"disambiguationData":[OSD([sQuery(id+"F0.wireOp",EDGE,"E11")])]});
            var sketch = newSketch(context, id + "F16", { "sketchPlane" : qUnion([Q0])});
            skCircle(sketch, "E49", {"center": v(13.5, 0) * mm, "radius": 1 * mm});
            skSolve(sketch);
        }
        {
            var Q0;
            Q0=makeQuery(id+"F16.imprint","IMPRINT",FACE,{"disambiguationData":[TD([[makeQuery(id+"F16.imprint","IMPRINT",EDGE,{"derivedFrom":sQuery(id+"F16.wireOp",EDGE,"E49")}),1.0]])]});
            extrude(context, id + "F17", {"entities" : qUnion([Q0]), "operationType" : NewBodyOperationType.REMOVE, "oppositeDirection" : true, "depth" : 25 * mm});
        }
        {
            var Q0;
            Q0=makeQuery(id+"F1.opRevolve","SWEPT_FACE",FACE,{"disambiguationData":[OSD([sQuery(id+"F0.wireOp",EDGE,"E7")])]});
            var sketch = newSketch(context, id + "F18", { "sketchPlane" : qUnion([Q0])});
            skCircle(sketch, "E50", {"center": v(-1.56, -8.86) * mm, "radius": 1.5 * mm});
            skCircle(sketch, "E51", {"center": v(-5.79, 6.9) * mm, "radius": 1.25 * mm});
            skLineSegment(sketch, "E52", {"start": v(-5.79, 6.9) * mm, "end": v(0, 0) * mm, "construction": true});
            skLineSegment(sketch, "E53", {"start": v(0, 0) * mm, "end": v(-1.56, -8.86) * mm, "construction": true});
            skSolve(sketch);
        }
        {
            var Q0;
            {Q0=qUnion([makeQuery(id+"F18.imprint","IMPRINT",FACE,{"disambiguationData":[TD([[makeQuery(id+"F18.imprint","IMPRINT",EDGE,{"derivedFrom":sQuery(id+"F18.wireOp",EDGE,"E50")}),1.0]])]}),makeQuery(id+"F18.imprint","IMPRINT",FACE,{"disambiguationData":[TD([[makeQuery(id+"F18.imprint","IMPRINT",EDGE,{"derivedFrom":sQuery(id+"F18.wireOp",EDGE,"E51")}),1.0]])]})]);}
            extrude(context, id + "F19", {"entities" : qUnion([Q0]), "operationType" : NewBodyOperationType.ADD, "depth" : 1.2 * mm});
        }
        {
            var Q0;
            Q0=makeQuery(id+"F19.opExtrude","CAP_FACE",FACE,{"disambiguationData":[OSD([sQuery(id+"F18.wireOp",EDGE,"E51")])],"isStart":false});
            var sketch = newSketch(context, id + "F20", { "sketchPlane" : qUnion([Q0])});
            skCircle(sketch, "E54", {"center": v(-5.79, 6.9) * mm, "radius": 0.75 * mm});
            skSolve(sketch);
        }
        {
            var Q0;
            Q0=makeQuery(id+"F20.imprint","IMPRINT",FACE,{"disambiguationData":[TD([[makeQuery(id+"F20.imprint","IMPRINT",EDGE,{"derivedFrom":sQuery(id+"F20.wireOp",EDGE,"E54")}),1.0]])]});
            extrude(context, id + "F21", {"entities" : qUnion([Q0]), "operationType" : NewBodyOperationType.ADD, "depth" : 2.1 * mm});
        }
        {
            var Q0;
            Q0=makeQuery(id+"F19.opExtrude","CAP_FACE",FACE,{"disambiguationData":[OSD([sQuery(id+"F18.wireOp",EDGE,"E50")])],"isStart":false});
            var sketch = newSketch(context, id + "F22", { "sketchPlane" : qUnion([Q0])});
            skLineSegment(sketch, "E55", {"start": v(0, 0) * mm, "end": v(-1.82, -10.34) * mm, "construction": true});
            skLineSegment(sketch, "E56", {"start": v(-2.35, -7.59) * mm, "end": v(-2.74, -9.8) * mm});
            skLineSegment(sketch, "E57", {"start": v(-0.38, -7.94) * mm, "end": v(-0.77, -10.14) * mm});
            skSolve(sketch);
        }
        {
            var Q0;
            {var subQ2=sQuery(id+"F22.wireOp",EDGE,"E56");Q0=makeQuery(id+"F22.imprint","IMPRINT",FACE,{"disambiguationData":[TD([[makeQuery(id+"F22.imprint","IMPRINT",EDGE,{"derivedFrom":subQ2}),1.0]])]});}
            extrude(context, id + "F23", {"entities" : qUnion([Q0]), "operationType" : NewBodyOperationType.ADD, "depth" : 2.1 * mm});
        }
        {
            var Q0;
            Q0=makeQuery(id+"F23.opExtrude","CAP_EDGE",EDGE,{"disambiguationData":[OSD([sQuery(id+"F22.wireOp",EDGE,"E56")])],"isStart":false});
            var Q1;
            Q1=makeQuery(id+"F23.opExtrude","CAP_EDGE",EDGE,{"disambiguationData":[OSD([sQuery(id+"F22.wireOp",EDGE,"E57")])],"isStart":false});
            chamfer(context, id + "F24", {"entities" : qUnion([Q0, Q1]), "chamferType" : ChamferType.OFFSET_ANGLE, "width" : 0.25 * mm, "oppositeDirection" : true, "angle" : 30 * degree, "tangentPropagation" : true});
        }
        {
            var Q0;
            Q0=makeQuery(id+"F1.opRevolve","SWEPT_FACE",FACE,{"disambiguationData":[OSD([sQuery(id+"F0.wireOp",EDGE,"E13")])]});
            var sketch = newSketch(context, id + "F25", { "sketchPlane" : qUnion([Q0])});
            skCircle(sketch, "E58", {"center": v(15.84, 4.24) * mm, "radius": 0.38 * mm});
            skLineSegment(sketch, "E59", {"start": v(0, 0) * mm, "end": v(15.84, 4.24) * mm, "construction": true});
            skCircle(sketch, "E60", {"center": v(0, 0) * mm, "radius": 16.4 * mm, "construction": true});
            skLineSegment(sketch, "E61", {"start": v(0, 0) * mm, "end": v(-5.6, -15.41) * mm, "construction": true});
            skLineSegment(sketch, "E62", {"start": v(-5.6, -15.41) * mm, "end": v(0, 0) * mm, "construction": true});
            skLineSegment(sketch, "E63", {"start": v(0, 0) * mm, "end": v(-13.43, 9.4) * mm, "construction": true});
            skCircle(sketch, "E64", {"center": v(-13.43, 9.4) * mm, "radius": 0.38 * mm});
            skCircle(sketch, "E65", {"center": v(-5.6, -15.41) * mm, "radius": 0.38 * mm});
            skSolve(sketch);
        }
        {
            var Q0;
            Q0=makeQuery(id+"F25.imprint","IMPRINT",FACE,{"disambiguationData":[TD([[makeQuery(id+"F25.imprint","IMPRINT",EDGE,{"derivedFrom":sQuery(id+"F25.wireOp",EDGE,"E58")}),1.0]])]});
            var Q1;
            Q1=makeQuery(id+"F25.imprint","IMPRINT",FACE,{"disambiguationData":[TD([[makeQuery(id+"F25.imprint","IMPRINT",EDGE,{"derivedFrom":sQuery(id+"F25.wireOp",EDGE,"E65")}),1.0]])]});
            var Q2;
            Q2=makeQuery(id+"F25.imprint","IMPRINT",FACE,{"disambiguationData":[TD([[makeQuery(id+"F25.imprint","IMPRINT",EDGE,{"derivedFrom":sQuery(id+"F25.wireOp",EDGE,"E64")}),1.0]])]});
            var Q3;
            Q3=sQuery(id+"F25.wireOp",EDGE,"E58");
            extrude(context, id + "F26", {"entities" : qUnion([Q0, Q1, Q2]), "surfaceEntities" : qUnion([Q3]), "oppositeDirection" : true, "depth" : 5 * mm});
        }
        {
            var Q0;
            Q0=makeQuery(id+"F26.opExtrude","SWEPT_BODY",BODY,{"disambiguationData":[OSD([sQuery(id+"F25.wireOp",EDGE,"E58")])]});
            var Q1;
            Q1=makeQuery(id+"F26.opExtrude","SWEPT_BODY",BODY,{"disambiguationData":[OSD([sQuery(id+"F25.wireOp",EDGE,"E64")])]});
            var Q2;
            Q2=makeQuery(id+"F26.opExtrude","SWEPT_BODY",BODY,{"disambiguationData":[OSD([sQuery(id+"F25.wireOp",EDGE,"E65")])]});
            var Q3;
            Q3=makeQuery(id+"F1.opRevolve","SWEPT_BODY",BODY,{"disambiguationData":[OSD([sQuery(id+"F0.wireOp",EDGE,"E0"),sQuery(id+"F0.wireOp",EDGE,"E1"),sQuery(id+"F0.wireOp",EDGE,"E2"),sQuery(id+"F0.wireOp",EDGE,"E3"),sQuery(id+"F0.wireOp",EDGE,"E4"),sQuery(id+"F0.wireOp",EDGE,"E5"),sQuery(id+"F0.wireOp",EDGE,"E6"),sQuery(id+"F0.wireOp",EDGE,"E7"),sQuery(id+"F0.wireOp",EDGE,"E8"),sQuery(id+"F0.wireOp",EDGE,"E9"),sQuery(id+"F0.wireOp",EDGE,"E10"),sQuery(id+"F0.wireOp",EDGE,"E11"),sQuery(id+"F0.wireOp",EDGE,"E12"),sQuery(id+"F0.wireOp",EDGE,"E13"),sQuery(id+"F0.wireOp",EDGE,"E14"),sQuery(id+"F0.wireOp",EDGE,"E15"),sQuery(id+"F0.wireOp",EDGE,"E16"),sQuery(id+"F0.wireOp",EDGE,"E17"),sQuery(id+"F0.wireOp",EDGE,"E18"),sQuery(id+"F0.wireOp",EDGE,"E19"),sQuery(id+"F0.wireOp",EDGE,"E20"),sQuery(id+"F0.wireOp",EDGE,"E21"),sQuery(id+"F0.wireOp",EDGE,"E22"),sQuery(id+"F0.wireOp",EDGE,"E23"),sQuery(id+"F0.wireOp",EDGE,"E24"),sQuery(id+"F0.wireOp",EDGE,"E25"),sQuery(id+"F0.wireOp",EDGE,"E26"),sQuery(id+"F0.wireOp",EDGE,"E27"),sQuery(id+"F0.wireOp",EDGE,"E28"),sQuery(id+"F0.wireOp",EDGE,"E29"),sQuery(id+"F0.wireOp",EDGE,"E30"),sQuery(id+"F0.wireOp",EDGE,"E31"),sQuery(id+"F0.wireOp",EDGE,"E32"),sQuery(id+"F0.wireOp",EDGE,"E33"),sQuery(id+"F0.wireOp",EDGE,"E34"),sQuery(id+"F0.wireOp",EDGE,"E35"),sQuery(id+"F0.wireOp",EDGE,"E36"),sQuery(id+"F0.wireOp",EDGE,"E37")])]});
            booleanBodies(context, id + "F27", {"operationType" : BooleanOperationType.SUBTRACTION, "tools" : qUnion([Q0, Q1, Q2]), "targets" : qUnion([Q3])});
        }
        {
            var Q0;
            Q0=makeQuery(id+"F1.opRevolve","SWEPT_FACE",FACE,{"disambiguationData":[OSD([sQuery(id+"F0.wireOp",EDGE,"E9")])]});
            cPlane(context, id + "F28", {"entities" : qUnion([Q0]), "cplaneType" : CPlaneType.OFFSET, "offset" : 2 * mm, "oppositeDirection" : true, "width" : 150 * mm, "height" : 150 * mm});
        }
        {
            var Q0;
            Q0=qCreatedBy(id+"F28.planeOp",FACE);
            var sketch = newSketch(context, id + "F29", { "sketchPlane" : qUnion([Q0])});
            skLineSegment(sketch, "E66", {"start": v(0, 0) * mm, "end": v(21.61, -7.87) * mm, "construction": true});
            skLineSegment(sketch, "E67", {"start": v(21.61, -7.87) * mm, "end": v(21.78, -7.42) * mm});
            skLineSegment(sketch, "E68", {"start": v(21.78, -7.42) * mm, "end": v(17.26, -5.78) * mm});
            skLineSegment(sketch, "E69", {"start": v(17.26, -5.78) * mm, "end": v(17.1, -6.22) * mm});
            skLineSegment(sketch, "E70", {"start": v(17.1, -6.22) * mm, "end": v(21.61, -7.87) * mm});
            skSolve(sketch);
        }
        {
            var Q0;
            Q0=makeQuery(id+"F29.imprint","IMPRINT",FACE,{"disambiguationData":[TD([[makeQuery(id+"F29.imprint","IMPRINT",EDGE,{"derivedFrom":sQuery(id+"F29.wireOp",EDGE,"E67")}),1.0]])]});
            var Q1;
            Q1=sQuery(id+"F29.wireOp",EDGE,"E66");
            revolve(context, id + "F30", {"entities" : qUnion([Q0]), "axis" : qUnion([Q1]), "revolveType" : RevolveType.FULL});
        }
        {
            var Q0;
            Q0=makeQuery(id+"F30.opRevolve","SWEPT_BODY",BODY,{"disambiguationData":[OSD([sQuery(id+"F29.wireOp",EDGE,"E67"),sQuery(id+"F29.wireOp",EDGE,"E68"),sQuery(id+"F29.wireOp",EDGE,"E69"),sQuery(id+"F29.wireOp",EDGE,"E70")])]});
            var Q1;
            Q1=sQuery(id+"F0.wireOp",EDGE,"E38");
            circularPattern(context, id + "F31", {"entities" : qUnion([Q0]), "axis" : qUnion([Q1]), "angle" : 96 * degree, "instanceCount" : 2, "oppositeDirection" : true});
        }
        {
            var Q0;
            Q0=makeQuery(id+"F31.opPattern","COPY",BODY,{"derivedFrom":makeQuery(id+"F30.opRevolve","SWEPT_BODY",BODY,{"disambiguationData":[OSD([sQuery(id+"F29.wireOp",EDGE,"E67"),sQuery(id+"F29.wireOp",EDGE,"E68"),sQuery(id+"F29.wireOp",EDGE,"E69"),sQuery(id+"F29.wireOp",EDGE,"E70")])]}),"instanceName":"1"});
            var Q1;
            Q1=sQuery(id+"F0.wireOp",EDGE,"E38");
            circularPattern(context, id + "F32", {"entities" : qUnion([Q0]), "axis" : qUnion([Q1]), "angle" : 84 * degree, "instanceCount" : 2, "oppositeDirection" : true});
        }
        {
            var Q0;
            Q0=makeQuery(id+"F30.opRevolve","SWEPT_BODY",BODY,{"disambiguationData":[OSD([sQuery(id+"F29.wireOp",EDGE,"E67"),sQuery(id+"F29.wireOp",EDGE,"E68"),sQuery(id+"F29.wireOp",EDGE,"E69"),sQuery(id+"F29.wireOp",EDGE,"E70")])]});
            var Q1;
            Q1=makeQuery(id+"F31.opPattern","COPY",BODY,{"derivedFrom":makeQuery(id+"F30.opRevolve","SWEPT_BODY",BODY,{"disambiguationData":[OSD([sQuery(id+"F29.wireOp",EDGE,"E67"),sQuery(id+"F29.wireOp",EDGE,"E68"),sQuery(id+"F29.wireOp",EDGE,"E69"),sQuery(id+"F29.wireOp",EDGE,"E70")])]}),"instanceName":"1"});
            var Q2;
            Q2=makeQuery(id+"F32.opPattern","COPY",BODY,{"derivedFrom":makeQuery(id+"F31.opPattern","COPY",BODY,{"derivedFrom":makeQuery(id+"F30.opRevolve","SWEPT_BODY",BODY,{"disambiguationData":[OSD([sQuery(id+"F29.wireOp",EDGE,"E67"),sQuery(id+"F29.wireOp",EDGE,"E68"),sQuery(id+"F29.wireOp",EDGE,"E69"),sQuery(id+"F29.wireOp",EDGE,"E70")])]}),"instanceName":"1"}),"instanceName":"1"});
            var Q3;
            Q3=makeQuery(id+"F1.opRevolve","SWEPT_BODY",BODY,{"disambiguationData":[OSD([sQuery(id+"F0.wireOp",EDGE,"E0"),sQuery(id+"F0.wireOp",EDGE,"E1"),sQuery(id+"F0.wireOp",EDGE,"E2"),sQuery(id+"F0.wireOp",EDGE,"E3"),sQuery(id+"F0.wireOp",EDGE,"E4"),sQuery(id+"F0.wireOp",EDGE,"E5"),sQuery(id+"F0.wireOp",EDGE,"E6"),sQuery(id+"F0.wireOp",EDGE,"E7"),sQuery(id+"F0.wireOp",EDGE,"E8"),sQuery(id+"F0.wireOp",EDGE,"E9"),sQuery(id+"F0.wireOp",EDGE,"E10"),sQuery(id+"F0.wireOp",EDGE,"E11"),sQuery(id+"F0.wireOp",EDGE,"E12"),sQuery(id+"F0.wireOp",EDGE,"E13"),sQuery(id+"F0.wireOp",EDGE,"E14"),sQuery(id+"F0.wireOp",EDGE,"E15"),sQuery(id+"F0.wireOp",EDGE,"E16"),sQuery(id+"F0.wireOp",EDGE,"E17"),sQuery(id+"F0.wireOp",EDGE,"E18"),sQuery(id+"F0.wireOp",EDGE,"E19"),sQuery(id+"F0.wireOp",EDGE,"E20"),sQuery(id+"F0.wireOp",EDGE,"E21"),sQuery(id+"F0.wireOp",EDGE,"E22"),sQuery(id+"F0.wireOp",EDGE,"E23"),sQuery(id+"F0.wireOp",EDGE,"E24"),sQuery(id+"F0.wireOp",EDGE,"E25"),sQuery(id+"F0.wireOp",EDGE,"E26"),sQuery(id+"F0.wireOp",EDGE,"E27"),sQuery(id+"F0.wireOp",EDGE,"E28"),sQuery(id+"F0.wireOp",EDGE,"E29"),sQuery(id+"F0.wireOp",EDGE,"E30"),sQuery(id+"F0.wireOp",EDGE,"E31"),sQuery(id+"F0.wireOp",EDGE,"E32"),sQuery(id+"F0.wireOp",EDGE,"E33"),sQuery(id+"F0.wireOp",EDGE,"E34"),sQuery(id+"F0.wireOp",EDGE,"E35"),sQuery(id+"F0.wireOp",EDGE,"E36"),sQuery(id+"F0.wireOp",EDGE,"E37")])]});
            booleanBodies(context, id + "F33", {"operationType" : BooleanOperationType.SUBTRACTION, "tools" : qUnion([Q0, Q1, Q2]), "targets" : qUnion([Q3])});
        }
        {
            var Q0;
            Q0=qCreatedBy(makeId("Right.planeOp"),FACE);
            var sketch = newSketch(context, id + "F34", { "sketchPlane" : qUnion([Q0])});
            skCircle(sketch, "E71", {"center": v(0, 10) * mm, "radius": 1.25 * mm});
            skSolve(sketch);
        }
        {
            var Q0;
            Q0=makeQuery(id+"F34.imprint","IMPRINT",FACE,{"disambiguationData":[TD([[makeQuery(id+"F34.imprint","IMPRINT",EDGE,{"derivedFrom":sQuery(id+"F34.wireOp",EDGE,"E71")}),1.0]])]});
            extrude(context, id + "F35", {"entities" : qUnion([Q0]), "operationType" : NewBodyOperationType.REMOVE, "depth" : 5 * mm});
        }
        {
            var Q0;
            Q0=makeQuery(id+"F1.opRevolve","SWEPT_FACE",FACE,{"disambiguationData":[OSD([sQuery(id+"F0.wireOp",EDGE,"E23")])]});
            var sketch = newSketch(context, id + "F36", { "sketchPlane" : qUnion([Q0])});
            skCircle(sketch, "E72", {"center": v(19.5, 0) * mm, "radius": 0.5 * mm});
            skCircle(sketch, "E73.1.0", {"center": v(18.32, -6.67) * mm, "radius": 0.5 * mm});
            skCircle(sketch, "E73.2.0", {"center": v(14.94, -12.53) * mm, "radius": 0.5 * mm});
            skCircle(sketch, "E73.3.0", {"center": v(9.75, -16.89) * mm, "radius": 0.5 * mm});
            skCircle(sketch, "E73.4.0", {"center": v(3.39, -19.2) * mm, "radius": 0.5 * mm});
            skCircle(sketch, "E73.5.0", {"center": v(-3.39, -19.2) * mm, "radius": 0.5 * mm});
            skCircle(sketch, "E73.6.0", {"center": v(-9.75, -16.89) * mm, "radius": 0.5 * mm});
            skCircle(sketch, "E73.7.0", {"center": v(-14.94, -12.53) * mm, "radius": 0.5 * mm});
            skPoint(sketch, "E73.center", {"position": v(0, 0) * mm});
            skLineSegment(sketch, "E73.anchor1", {"start": v(0, 0) * mm, "end": v(19.5, 0) * mm, "construction": true});
            skLineSegment(sketch, "E73.anchor2", {"start": v(0, 0) * mm, "end": v(-14.94, -12.53) * mm, "construction": true});
            skSolve(sketch);
        }
        {
            var Q0;
            {Q0=qUnion([makeQuery(id+"F36.imprint","IMPRINT",FACE,{"disambiguationData":[TD([[makeQuery(id+"F36.imprint","IMPRINT",EDGE,{"derivedFrom":sQuery(id+"F36.wireOp",EDGE,"E72")}),1.0]])]}),makeQuery(id+"F36.imprint","IMPRINT",FACE,{"disambiguationData":[TD([[makeQuery(id+"F36.imprint","IMPRINT",EDGE,{"derivedFrom":sQuery(id+"F36.wireOp",EDGE,"E73.1.0")}),1.0]])]}),makeQuery(id+"F36.imprint","IMPRINT",FACE,{"disambiguationData":[TD([[makeQuery(id+"F36.imprint","IMPRINT",EDGE,{"derivedFrom":sQuery(id+"F36.wireOp",EDGE,"E73.2.0")}),1.0]])]}),makeQuery(id+"F36.imprint","IMPRINT",FACE,{"disambiguationData":[TD([[makeQuery(id+"F36.imprint","IMPRINT",EDGE,{"derivedFrom":sQuery(id+"F36.wireOp",EDGE,"E73.3.0")}),1.0]])]}),makeQuery(id+"F36.imprint","IMPRINT",FACE,{"disambiguationData":[TD([[makeQuery(id+"F36.imprint","IMPRINT",EDGE,{"derivedFrom":sQuery(id+"F36.wireOp",EDGE,"E73.4.0")}),1.0]])]}),makeQuery(id+"F36.imprint","IMPRINT",FACE,{"disambiguationData":[TD([[makeQuery(id+"F36.imprint","IMPRINT",EDGE,{"derivedFrom":sQuery(id+"F36.wireOp",EDGE,"E73.5.0")}),1.0]])]}),makeQuery(id+"F36.imprint","IMPRINT",FACE,{"disambiguationData":[TD([[makeQuery(id+"F36.imprint","IMPRINT",EDGE,{"derivedFrom":sQuery(id+"F36.wireOp",EDGE,"E73.6.0")}),1.0]])]}),makeQuery(id+"F36.imprint","IMPRINT",FACE,{"disambiguationData":[TD([[makeQuery(id+"F36.imprint","IMPRINT",EDGE,{"derivedFrom":sQuery(id+"F36.wireOp",EDGE,"E73.7.0")}),1.0]])]})]);}
            extrude(context, id + "F37", {"entities" : qUnion([Q0]), "operationType" : NewBodyOperationType.REMOVE, "oppositeDirection" : true, "depth" : 2.5 * mm});
        }
        {
            var Q0;
            Q0=makeQuery(id+"F1.opRevolve","SWEPT_FACE",FACE,{"disambiguationData":[OSD([sQuery(id+"F0.wireOp",EDGE,"E23")])]});
            var sketch = newSketch(context, id + "F38", { "sketchPlane" : qUnion([Q0])});
            skLineSegment(sketch, "E74", {"start": v(0, 0) * mm, "end": v(17.62, 7.12) * mm, "construction": true});
            skCircle(sketch, "E75", {"center": v(17.62, 7.12) * mm, "radius": 1 * mm});
            skCircle(sketch, "E76.1.0", {"center": v(5.87, 18.07) * mm, "radius": 1 * mm});
            skPoint(sketch, "E76.center", {"position": v(0, 0) * mm});
            skLineSegment(sketch, "E76.anchor2", {"start": v(0, 0) * mm, "end": v(5.87, 18.07) * mm, "construction": true});
            skCircle(sketch, "E77.1.0", {"center": v(-12.71, 14.12) * mm, "radius": 1 * mm});
            skLineSegment(sketch, "E77.anchor2", {"start": v(0, 0) * mm, "end": v(-12.71, 14.12) * mm, "construction": true});
            skCircle(sketch, "E78.1.0", {"center": v(-17.62, -7.12) * mm, "radius": 1 * mm});
            skLineSegment(sketch, "E78.anchor2", {"start": v(0, 0) * mm, "end": v(-17.62, -7.12) * mm, "construction": true});
            skSolve(sketch);
        }
        {
            var Q0;
            {Q0=qUnion([makeQuery(id+"F38.imprint","IMPRINT",FACE,{"disambiguationData":[TD([[makeQuery(id+"F38.imprint","IMPRINT",EDGE,{"derivedFrom":sQuery(id+"F38.wireOp",EDGE,"E75")}),1.0]])]}),makeQuery(id+"F38.imprint","IMPRINT",FACE,{"disambiguationData":[TD([[makeQuery(id+"F38.imprint","IMPRINT",EDGE,{"derivedFrom":sQuery(id+"F38.wireOp",EDGE,"E76.1.0")}),1.0]])]}),makeQuery(id+"F38.imprint","IMPRINT",FACE,{"disambiguationData":[TD([[makeQuery(id+"F38.imprint","IMPRINT",EDGE,{"derivedFrom":sQuery(id+"F38.wireOp",EDGE,"E77.1.0")}),1.0]])]}),makeQuery(id+"F38.imprint","IMPRINT",FACE,{"disambiguationData":[TD([[makeQuery(id+"F38.imprint","IMPRINT",EDGE,{"derivedFrom":sQuery(id+"F38.wireOp",EDGE,"E78.1.0")}),1.0]])]})]);}
            extrude(context, id + "F39", {"entities" : qUnion([Q0]), "operationType" : NewBodyOperationType.REMOVE, "oppositeDirection" : true, "depth" : 2.5 * mm});
        }
        {
            var Q0;
            Q0=makeQuery(id+"F1.opRevolve","SWEPT_FACE",FACE,{"disambiguationData":[OSD([sQuery(id+"F0.wireOp",EDGE,"E23")])]});
            cPlane(context, id + "F40", {"entities" : qUnion([Q0]), "cplaneType" : CPlaneType.OFFSET, "offset" : 0.2 * mm, "width" : 150 * mm, "height" : 150 * mm});
        }
        {
            var Q0;
            Q0=qCreatedBy(id+"F40.planeOp",FACE);
            var sketch = newSketch(context, id + "F41", { "sketchPlane" : qUnion([Q0])});
            skLineSegment(sketch, "E79", {"start": v(0, 0) * mm, "end": v(2.2, 62.93) * mm, "construction": true});
            skLineSegment(sketch, "E80", {"start": v(0, 0) * mm, "end": v(60.82, 16.3) * mm, "construction": true});
            skLineSegment(sketch, "E81", {"start": v(2.2, 62.93) * mm, "end": v(0.2, 63) * mm, "construction": true});
            skCircle(sketch, "E82", {"center": v(0.2, 63) * mm, "radius": 50 * mm});
            skLineSegment(sketch, "E83", {"start": v(60.82, 16.3) * mm, "end": v(60.3, 18.23) * mm, "construction": true});
            skCircle(sketch, "E84", {"center": v(60.3, 18.23) * mm, "radius": 50 * mm});
            skSolve(sketch);
        }
        {
            var Q0;
            {var subQ0=sQuery(id+"F41.wireOp",EDGE,"E84");var subQ1=sQuery(id+"F41.wireOp",EDGE,"E82");var subQ3=makeQuery(id+"F41.imprint","INTERSECT",VERTEX,{"disambiguationData":[OD(0.0)],"derivedFrom":[subQ1,subQ0]});var subQ5=makeQuery(id+"F41.imprint","IMPRINT",EDGE,{"disambiguationData":[TD([[subQ3,-1.0]])],"derivedFrom":subQ1});Q0=qUnion([makeQuery(id+"F41.imprint","IMPRINT",FACE,{"disambiguationData":[TD([[makeQuery(id+"F41.imprint","IMPRINT",EDGE,{"disambiguationData":[TD([[subQ3,1.0]])],"derivedFrom":subQ1}),1.0]])]}),makeQuery(id+"F41.imprint","IMPRINT",FACE,{"disambiguationData":[TD([[subQ5,-1.0]])]}),makeQuery(id+"F41.imprint","IMPRINT",FACE,{"disambiguationData":[TD([[subQ5,1.0]])]})]);}
            extrude(context, id + "F42", {"entities" : qUnion([Q0]), "operationType" : NewBodyOperationType.REMOVE, "depth" : 5 * mm});
        }
    });
